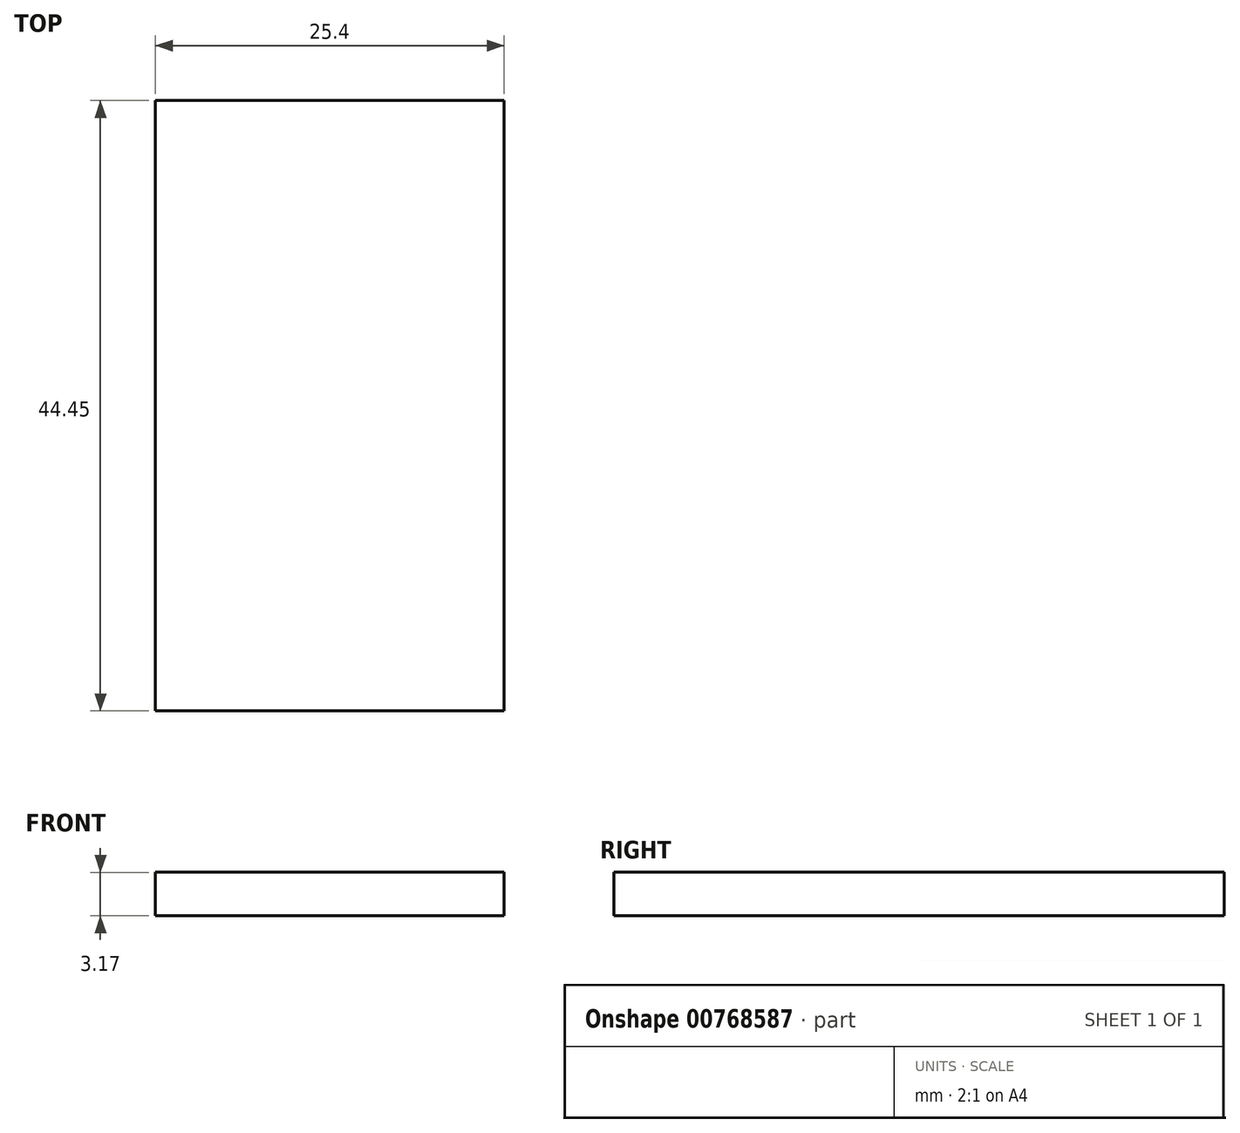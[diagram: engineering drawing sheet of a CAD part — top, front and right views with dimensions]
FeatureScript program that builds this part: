
annotation { "Feature Type Name" : "Feature", "Feature Type Description" : "" }
export const myFeature = defineFeature(function(context is Context, id is Id, definition is map)
    precondition{}
    {
        {
            var Q0;
            Q0=qCreatedBy(makeId("Top.planeOp"),FACE);
            var sketch = newSketch(context, id + "F0", { "sketchPlane" : qUnion([Q0])});
            skLineSegment(sketch, "E0.bottom", {"start": v(-25.4, 0) * mm, "end": v(0, 0) * mm});
            skLineSegment(sketch, "E0.top", {"start": v(-25.4, 44.45) * mm, "end": v(0, 44.45) * mm});
            skLineSegment(sketch, "E0.left", {"start": v(-25.4, 0) * mm, "end": v(-25.4, 44.45) * mm});
            skLineSegment(sketch, "E0.right", {"start": v(0, 0) * mm, "end": v(0, 44.45) * mm});
            skSolve(sketch);
        }
        {
            var Q0;
            Q0=makeQuery(id+"F0.imprint","IMPRINT",FACE,{"disambiguationData":[TD([[makeQuery(id+"F0.imprint","IMPRINT",EDGE,{"derivedFrom":sQuery(id+"F0.wireOp",EDGE,"E0.bottom")}),1.0]])]});
            extrude(context, id + "F1", {"entities" : qUnion([Q0]), "depth" : 3.17 * mm, "offsetDistance" : 25.4 * mm});
        }
    });
